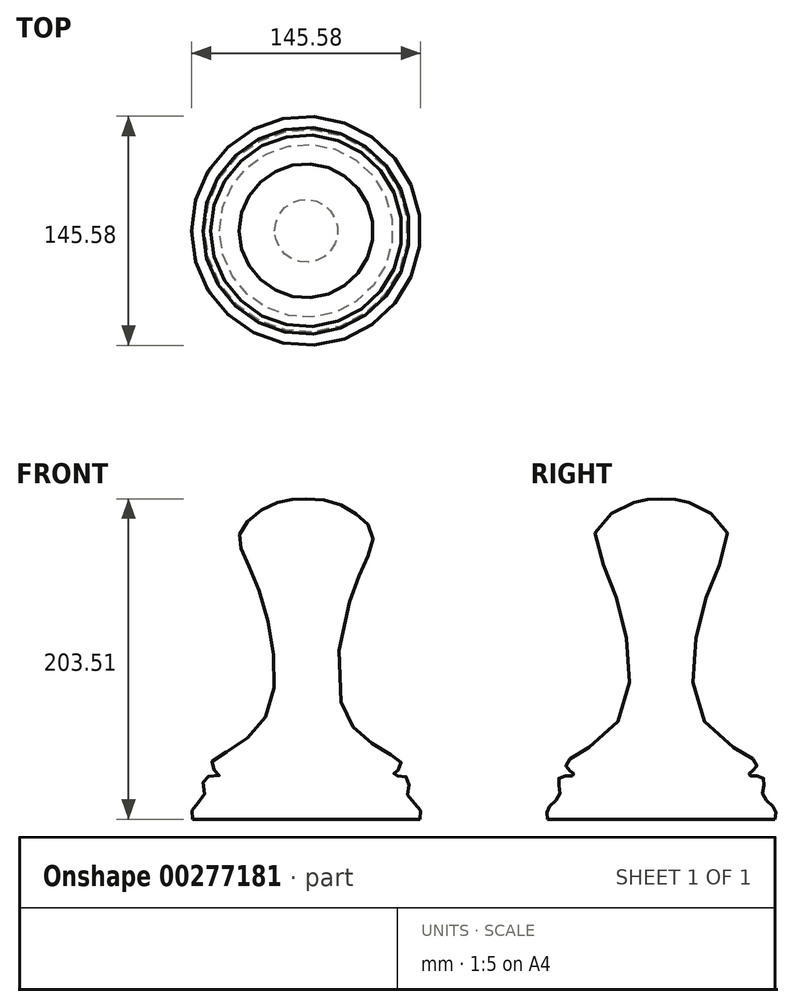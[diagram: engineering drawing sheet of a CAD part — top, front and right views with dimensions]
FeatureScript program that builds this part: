
annotation { "Feature Type Name" : "Feature", "Feature Type Description" : "" }
export const myFeature = defineFeature(function(context is Context, id is Id, definition is map)
    precondition{}
    {
        {
            var Q0;
            Q0=qCreatedBy(makeId("Front.planeOp"),FACE);
            var sketch = newSketch(context, id + "F0", { "sketchPlane" : qUnion([Q0])});
            skLineSegment(sketch, "E0", {"start": v(0, 102.02) * mm, "end": v(0, -101.18) * mm, "construction": true});
            skFitSpline(sketch, "E1", {"points": [v(0, 102.02) * mm, v(-20.57, 98.73) * mm, v(-41.84, 80.84) * mm, v(-32.72, 50.79) * mm, v(-28.33, -40.71) * mm, v(-60.74, -67.38) * mm, v(-55, -73.46) * mm, v(-64.8, -75.15) * mm, v(-64.46, -85.62) * mm, v(-71.89, -94.4) * mm, v(-72.22, -101.49) * mm], "startDerivative": vector(-200.59, -4.84) * mm, "endDerivative": vector(28.22, -129.97) * mm});
            skLineSegment(sketch, "E2", {"start": v(0, 102.02) * mm, "end": v(0, -101.18) * mm});
            skLineSegment(sketch, "E3", {"start": v(-72.22, -101.49) * mm, "end": v(0, -101.18) * mm});
            skSolve(sketch);
        }
        {
            var Q0;
            Q0=makeQuery(id+"F0.imprint","IMPRINT",FACE,{"disambiguationData":[TD([[makeQuery(id+"F0.imprint","IMPRINT",EDGE,{"derivedFrom":sQuery(id+"F0.wireOp",EDGE,"E1")}),1.0]])]});
            var Q1;
            Q1=sQuery(id+"F0.wireOp",EDGE,"E2");
            revolve(context, id + "F1", {"entities" : qUnion([Q0]), "axis" : qUnion([Q1]), "revolveType" : RevolveType.FULL});
        }
    });
